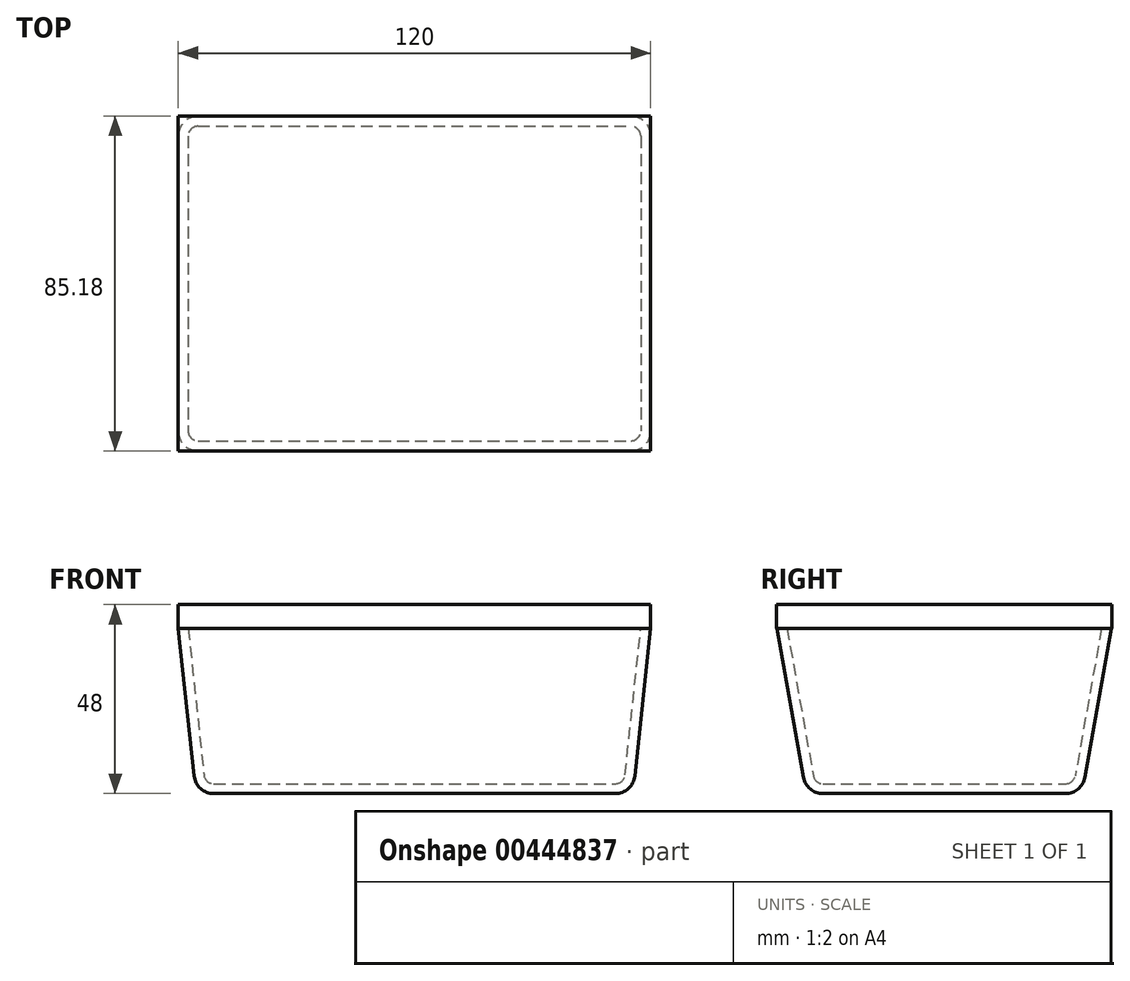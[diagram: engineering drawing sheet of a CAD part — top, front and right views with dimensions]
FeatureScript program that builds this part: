
annotation { "Feature Type Name" : "Feature", "Feature Type Description" : "" }
export const myFeature = defineFeature(function(context is Context, id is Id, definition is map)
    precondition{}
    {
        {
            var Q0;
            Q0=qCreatedBy(makeId("Top.planeOp"),FACE);
            var sketch = newSketch(context, id + "F0", { "sketchPlane" : qUnion([Q0])});
            skLineSegment(sketch, "E0.bottom", {"start": v(-55.5, -35) * mm, "end": v(55.5, -35) * mm});
            skLineSegment(sketch, "E0.top", {"start": v(-55.5, 35) * mm, "end": v(55.5, 35) * mm});
            skLineSegment(sketch, "E0.left", {"start": v(-55.5, -35) * mm, "end": v(-55.5, 35) * mm});
            skLineSegment(sketch, "E0.right", {"start": v(55.5, -35) * mm, "end": v(55.5, 35) * mm});
            skPoint(sketch, "E0.middle", {"position": v(0, 0) * mm});
            skSolve(sketch);
        }
        {
            var Q0;
            Q0=makeQuery(id+"F0.imprint","IMPRINT",FACE,{"disambiguationData":[TD([[makeQuery(id+"F0.imprint","IMPRINT",EDGE,{"derivedFrom":sQuery(id+"F0.wireOp",EDGE,"E0.bottom")}),1.0]])]});
            cPlane(context, id + "F1", {"entities" : qUnion([Q0]), "cplaneType" : CPlaneType.OFFSET, "offset" : 42 * mm, "width" : 150 * mm, "height" : 150 * mm});
        }
        {
            var Q0;
            Q0=qCreatedBy(id+"F1.planeOp",FACE);
            var sketch = newSketch(context, id + "F2", { "sketchPlane" : qUnion([Q0])});
            skLineSegment(sketch, "E1.bottom", {"start": v(-60, 42.5) * mm, "end": v(60, 42.5) * mm});
            skLineSegment(sketch, "E1.top", {"start": v(-60, -42.5) * mm, "end": v(60, -42.5) * mm});
            skLineSegment(sketch, "E1.left", {"start": v(-60, 42.5) * mm, "end": v(-60, -42.5) * mm});
            skLineSegment(sketch, "E1.right", {"start": v(60, 42.5) * mm, "end": v(60, -42.5) * mm});
            skPoint(sketch, "E1.middle", {"position": v(0, 0) * mm});
            skSolve(sketch);
        }
        {
            var Q0;
            Q0=makeQuery(id+"F2.imprint","IMPRINT",FACE,{"disambiguationData":[TD([[makeQuery(id+"F2.imprint","IMPRINT",EDGE,{"derivedFrom":sQuery(id+"F2.wireOp",EDGE,"E1.bottom")}),-1.0]])]});
            var Q1;
            Q1=makeQuery(id+"F0.imprint","IMPRINT",FACE,{"disambiguationData":[TD([[makeQuery(id+"F0.imprint","IMPRINT",EDGE,{"derivedFrom":sQuery(id+"F0.wireOp",EDGE,"E0.bottom")}),1.0]])]});
            loft(context, id + "F3", {"sheetProfilesArray" : [{ "sheetProfileEntities" : qUnion([Q0]) }, { "sheetProfileEntities" : qUnion([Q1]) }]});
        }
        {
            var Q0;
            Q0=makeQuery(id+"F3.opLoft","SWEPT_EDGE",EDGE,{"disambiguationData":[OSD([sQuery(id+"F0.wireOp",EDGE,"E0.top"),sQuery(id+"F0.wireOp",EDGE,"E0.right"),sQuery(id+"F2.wireOp",EDGE,"E1.bottom"),sQuery(id+"F2.wireOp",EDGE,"E1.right")])]});
            fillet(context, id + "F4", {"entities" : qUnion([Q0]), "radius" : 5 * mm, "tangentPropagation" : true, "allowEdgeOverflow" : false});
        }
        {
            var Q0;
            Q0=makeQuery(id+"F3.opLoft","SWEPT_EDGE",EDGE,{"disambiguationData":[OSD([sQuery(id+"F0.wireOp",EDGE,"E0.bottom"),sQuery(id+"F0.wireOp",EDGE,"E0.right"),sQuery(id+"F2.wireOp",EDGE,"E1.top"),sQuery(id+"F2.wireOp",EDGE,"E1.right")])]});
            fillet(context, id + "F5", {"entities" : qUnion([Q0]), "radius" : 5 * mm, "tangentPropagation" : true, "allowEdgeOverflow" : false});
        }
        {
            var Q0;
            Q0=makeQuery(id+"F3.opLoft","MID_CAP_EDGE",EDGE,{"disambiguationData":[OSD([sQuery(id+"F0.wireOp",EDGE,"E0.bottom"),sQuery(id+"F0.wireOp",EDGE,"E0.left"),sQuery(id+"F0.wireOp",EDGE,"E0.right")])],"capPos":1.0});
            var Q1;
            Q1=makeQuery(id+"F3.opLoft","SWEPT_EDGE",EDGE,{"disambiguationData":[OSD([sQuery(id+"F0.wireOp",EDGE,"E0.bottom"),sQuery(id+"F0.wireOp",EDGE,"E0.left"),sQuery(id+"F2.wireOp",EDGE,"E1.top"),sQuery(id+"F2.wireOp",EDGE,"E1.left")])]});
            var Q2;
            Q2=makeQuery(id+"F3.opLoft","MID_CAP_EDGE",EDGE,{"disambiguationData":[OSD([sQuery(id+"F0.wireOp",EDGE,"E0.bottom"),sQuery(id+"F0.wireOp",EDGE,"E0.top"),sQuery(id+"F0.wireOp",EDGE,"E0.left")])],"capPos":1.0});
            var Q3;
            Q3=makeQuery(id+"F3.opLoft","SWEPT_EDGE",EDGE,{"disambiguationData":[OSD([sQuery(id+"F0.wireOp",EDGE,"E0.top"),sQuery(id+"F0.wireOp",EDGE,"E0.left"),sQuery(id+"F2.wireOp",EDGE,"E1.bottom"),sQuery(id+"F2.wireOp",EDGE,"E1.left")])]});
            fillet(context, id + "F6", {"entities" : qUnion([Q0, Q1, Q2, Q3]), "radius" : 5 * mm, "tangentPropagation" : true, "allowEdgeOverflow" : false});
        }
        {
            var Q0;
            Q0=makeQuery(id+"F3.opLoft","CAP_FACE",FACE,{"disambiguationData":[OSD([makeQuery(id+"F2.imprint","IMPRINT",FACE,{"disambiguationData":[TD([[makeQuery(id+"F2.imprint","IMPRINT",EDGE,{"derivedFrom":sQuery(id+"F2.wireOp",EDGE,"E1.bottom")}),-1.0]])]})])],"isStart":true});
            shell(context, id + "F7", {"entities" : qUnion([Q0]), "thickness" : 2.5 * mm});
        }
        {
            var Q0;
            Q0=qCreatedBy(id+"F1.planeOp",FACE);
            var sketch = newSketch(context, id + "F8", { "sketchPlane" : qUnion([Q0])});
            skLineSegment(sketch, "E2.bottom", {"start": v(-60, -42.59) * mm, "end": v(60, -42.59) * mm});
            skLineSegment(sketch, "E2.top", {"start": v(-60, 42.59) * mm, "end": v(60, 42.59) * mm});
            skLineSegment(sketch, "E2.left", {"start": v(-60, -42.59) * mm, "end": v(-60, 42.59) * mm});
            skLineSegment(sketch, "E2.right", {"start": v(60, -42.59) * mm, "end": v(60, 42.59) * mm});
            skPoint(sketch, "E2.middle", {"position": v(0, 0) * mm});
            skSolve(sketch);
        }
        {
            var Q0;
            Q0 = qSketchRegion(id + "F8", true);
            extrude(context, id + "F9", {"entities" : qUnion([Q0]), "operationType" : NewBodyOperationType.ADD, "depth" : 6 * mm});
        }
    });
